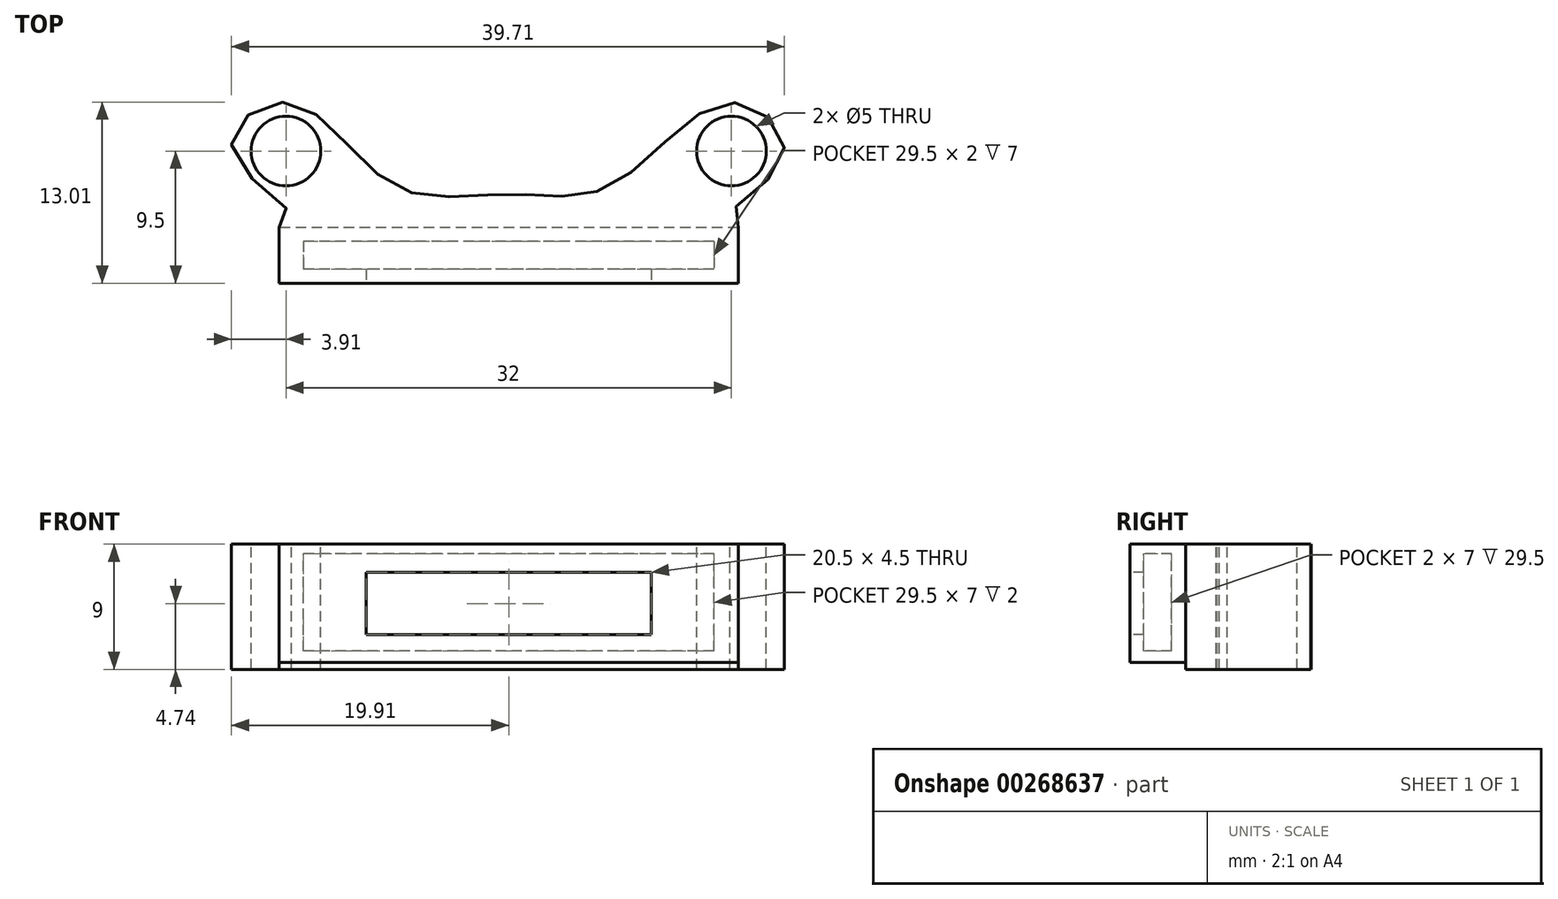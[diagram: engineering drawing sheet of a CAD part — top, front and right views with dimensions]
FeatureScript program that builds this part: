
annotation { "Feature Type Name" : "Feature", "Feature Type Description" : "" }
export const myFeature = defineFeature(function(context is Context, id is Id, definition is map)
    precondition{}
    {
        {
            var Q0;
            Q0=qCreatedBy(makeId("Top.planeOp"),FACE);
            var sketch = newSketch(context, id + "F0", { "sketchPlane" : qUnion([Q0])});
            skLineSegment(sketch, "E0.bottom", {"start": v(16.5, -1.5) * mm, "end": v(-16.5, -1.5) * mm});
            skLineSegment(sketch, "E0.top", {"start": v(16.5, 1.5) * mm, "end": v(-16.5, 1.5) * mm});
            skLineSegment(sketch, "E0.left", {"start": v(16.5, -1.5) * mm, "end": v(16.5, 1.5) * mm});
            skLineSegment(sketch, "E0.right", {"start": v(-16.5, -1.5) * mm, "end": v(-16.5, 1.5) * mm});
            skPoint(sketch, "E0.middle", {"position": v(0, 0) * mm});
            skFitSpline(sketch, "E1", {"points": [v(-16.5, 1.5) * mm, v(-19.68, 6.51) * mm, v(-15.96, 10.5) * mm, v(-8.4, 4.6) * mm, v(0, 3.92) * mm, v(7.53, 4.6) * mm, v(16.09, 10.5) * mm, v(19.56, 6.1) * mm, v(16.5, 1.5) * mm], "startDerivative": vector(76.87, 19.5) * mm, "endDerivative": vector(59.53, -29.95) * mm});
            skPoint(sketch, "E2", {"position": v(-16, 7) * mm});
            skPoint(sketch, "E3", {"position": v(16, 7) * mm});
            skSolve(sketch);
        }
        {
            var Q0;
            Q0=makeQuery(id+"F0.imprint","IMPRINT",FACE,{"disambiguationData":[TD([[makeQuery(id+"F0.imprint","IMPRINT",EDGE,{"derivedFrom":sQuery(id+"F0.wireOp",EDGE,"E0.bottom")}),-1.0]])]});
            extrude(context, id + "F1", {"entities" : qUnion([Q0]), "oppositeDirection" : true, "depth" : 8.5 * mm});
        }
        {
            var Q0;
            Q0=makeQuery(id+"F0.imprint","IMPRINT",FACE,{"disambiguationData":[TD([[makeQuery(id+"F0.imprint","IMPRINT",EDGE,{"derivedFrom":sQuery(id+"F0.wireOp",EDGE,"E0.top")}),-1.0]])]});
            extrude(context, id + "F2", {"entities" : qUnion([Q0]), "operationType" : NewBodyOperationType.ADD, "oppositeDirection" : true, "depth" : 9 * mm});
        }
        {
            var Q0;
            Q0=sQuery(id+"F0.wireOp",VERTEX,"E2");
            var Q1;
            Q1=sQuery(id+"F0.wireOp",VERTEX,"E3");
            var Q2;
            Q2=makeQuery(id+"F1.opExtrude","SWEPT_BODY",BODY,{"disambiguationData":[OSD([sQuery(id+"F0.wireOp",EDGE,"E0.bottom"),sQuery(id+"F0.wireOp",EDGE,"E0.top"),sQuery(id+"F0.wireOp",EDGE,"E0.left"),sQuery(id+"F0.wireOp",EDGE,"E0.right"),sQuery(id+"F0.wireOp",EDGE,"qSG4pFbB-mWNJ-fMbz-A37t-o3lnEbjPYmPd.bottom"),sQuery(id+"F0.wireOp",EDGE,"qSG4pFbB-mWNJ-fMbz-A37t-o3lnEbjPYmPd.top"),sQuery(id+"F0.wireOp",EDGE,"qSG4pFbB-mWNJ-fMbz-A37t-o3lnEbjPYmPd.left"),sQuery(id+"F0.wireOp",EDGE,"qSG4pFbB-mWNJ-fMbz-A37t-o3lnEbjPYmPd.right")])]});
            hole(context, id + "F3", {"style" : HoleStyle.SIMPLE, "endStyle" : HoleEndStyle.THROUGH, "holeDiameter" : 5 * mm, "tappedDepth" : 12 * mm, "tapClearance" : 3, "locations" : qUnion([Q0, Q1]), "scope" : qUnion([Q2])});
        }
        {
            var Q0;
            Q0=makeQuery(id+"F1.opExtrude","SWEPT_FACE",FACE,{"disambiguationData":[OSD([sQuery(id+"F0.wireOp",EDGE,"E0.bottom")])]});
            var sketch = newSketch(context, id + "F4", { "sketchPlane" : qUnion([Q0])});
            skLineSegment(sketch, "E4.bottom", {"start": v(14.75, -7.69) * mm, "end": v(-14.75, -7.69) * mm});
            skLineSegment(sketch, "E4.top", {"start": v(14.75, -0.69) * mm, "end": v(-14.75, -0.69) * mm});
            skLineSegment(sketch, "E4.left", {"start": v(14.75, -7.69) * mm, "end": v(14.75, -0.69) * mm});
            skLineSegment(sketch, "E4.right", {"start": v(-14.75, -7.69) * mm, "end": v(-14.75, -0.69) * mm});
            skPoint(sketch, "E4.middle", {"position": v(0, -4.19) * mm});
            skSolve(sketch);
        }
        {
            var Q0;
            Q0=makeQuery(id+"F4.imprint","IMPRINT",FACE,{"disambiguationData":[TD([[makeQuery(id+"F4.imprint","IMPRINT",EDGE,{"derivedFrom":sQuery(id+"F4.wireOp",EDGE,"E4.bottom")}),-1.0]])]});
            extrude(context, id + "F5", {"entities" : qUnion([Q0]), "operationType" : NewBodyOperationType.REMOVE, "oppositeDirection" : true, "depth" : 2 * mm});
        }
        {
            var Q0;
            Q0=makeQuery(id+"F1.opExtrude","SWEPT_FACE",FACE,{"disambiguationData":[OSD([sQuery(id+"F0.wireOp",EDGE,"E0.bottom")])]});
            var sketch = newSketch(context, id + "F6", { "sketchPlane" : qUnion([Q0])});
            skLineSegment(sketch, "E5.bottom", {"start": v(-16.5, 0) * mm, "end": v(16.5, 0) * mm});
            skLineSegment(sketch, "E5.top", {"start": v(-16.5, -8.5) * mm, "end": v(16.5, -8.5) * mm});
            skLineSegment(sketch, "E5.left", {"start": v(-16.5, 0) * mm, "end": v(-16.5, -8.5) * mm});
            skLineSegment(sketch, "E5.right", {"start": v(16.5, 0) * mm, "end": v(16.5, -8.5) * mm});
            skSolve(sketch);
        }
        {
            var Q0;
            Q0 = qSketchRegion(id + "F6", true);
            extrude(context, id + "F7", {"entities" : qUnion([Q0]), "operationType" : NewBodyOperationType.ADD, "depth" : 1 * mm});
        }
        {
            var Q0;
            Q0=makeQuery(id+"F7.opExtrude","CAP_FACE",FACE,{"disambiguationData":[OSD([sQuery(id+"F6.wireOp",EDGE,"E5.bottom"),sQuery(id+"F6.wireOp",EDGE,"E5.top"),sQuery(id+"F6.wireOp",EDGE,"E5.left"),sQuery(id+"F6.wireOp",EDGE,"E5.right")])],"isStart":false});
            var sketch = newSketch(context, id + "F8", { "sketchPlane" : qUnion([Q0])});
            skLineSegment(sketch, "E6.bottom", {"start": v(10.25, -6.5) * mm, "end": v(-10.25, -6.5) * mm});
            skLineSegment(sketch, "E6.top", {"start": v(10.25, -2) * mm, "end": v(-10.25, -2) * mm});
            skLineSegment(sketch, "E6.left", {"start": v(10.25, -6.5) * mm, "end": v(10.25, -2) * mm});
            skLineSegment(sketch, "E6.right", {"start": v(-10.25, -6.5) * mm, "end": v(-10.25, -2) * mm});
            skPoint(sketch, "E6.middle", {"position": v(0, -4.26) * mm});
            skSolve(sketch);
        }
        {
            var Q0;
            Q0=makeQuery(id+"F8.imprint","IMPRINT",FACE,{"disambiguationData":[TD([[makeQuery(id+"F8.imprint","IMPRINT",EDGE,{"derivedFrom":sQuery(id+"F8.wireOp",EDGE,"E6.bottom")}),-1.0]])]});
            extrude(context, id + "F9", {"entities" : qUnion([Q0]), "operationType" : NewBodyOperationType.REMOVE, "oppositeDirection" : true, "depth" : 2 * mm});
        }
    });
